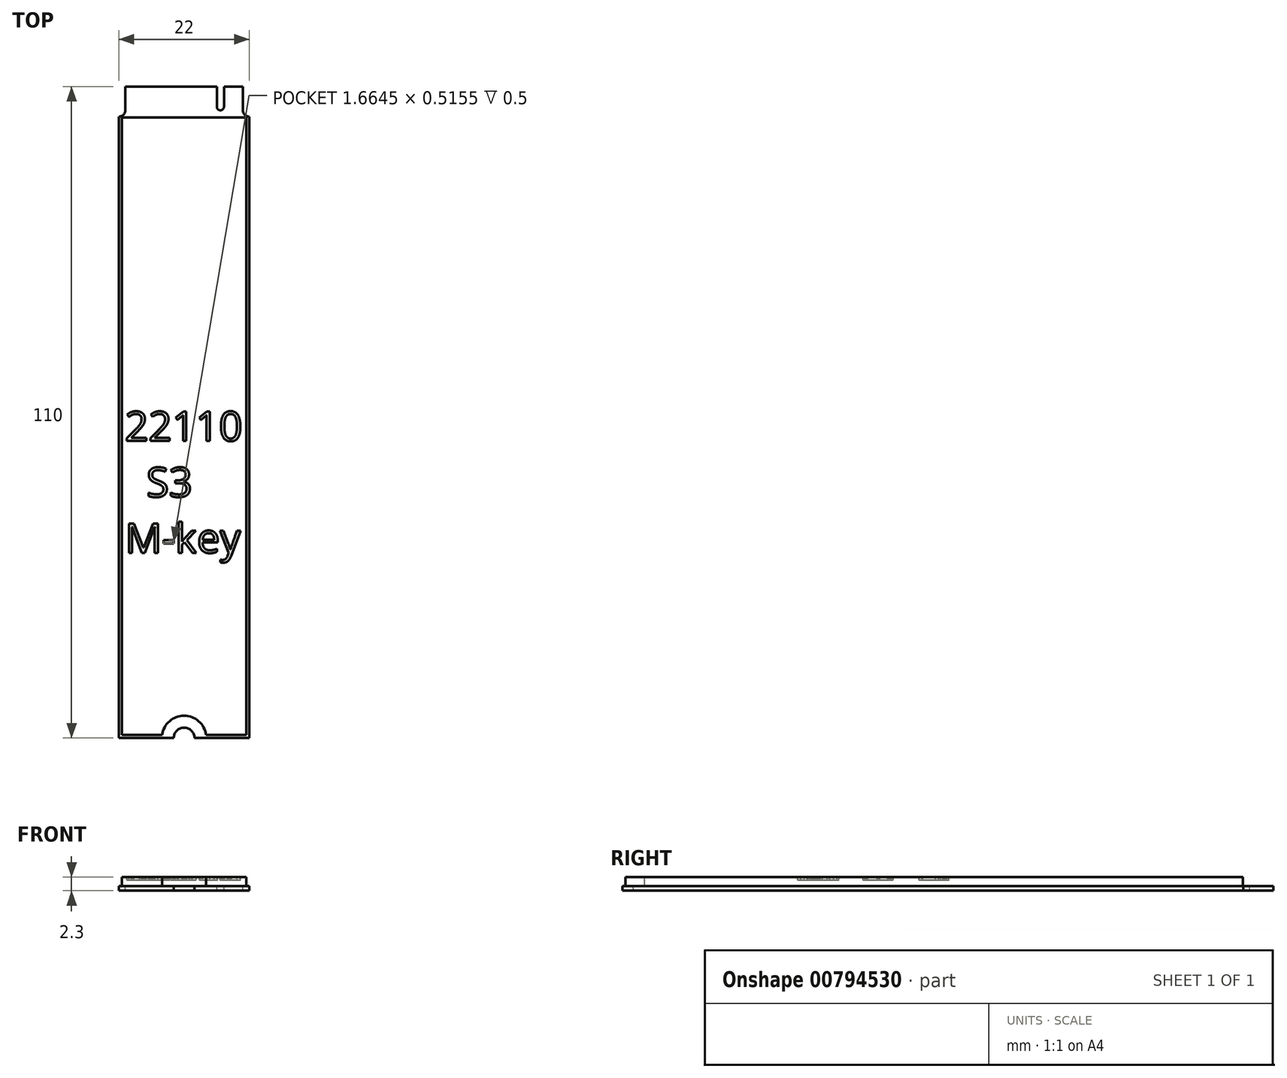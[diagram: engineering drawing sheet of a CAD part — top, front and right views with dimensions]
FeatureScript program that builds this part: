
annotation { "Feature Type Name" : "Feature", "Feature Type Description" : "" }
export const myFeature = defineFeature(function(context is Context, id is Id, definition is map)
    precondition{}
    {
        {
            assignVariable(context, id + "F0", {"name" : "thick", "anyValue" : .8});
        }
        {
            assignVariable(context, id + "F1", {"name" : "compheight", "anyValue" : 1.5});
        }
        {
            var Q0;
            Q0=qCreatedBy(makeId("Top.planeOp"),FACE);
            var sketch = newSketch(context, id + "F2", { "sketchPlane" : qUnion([Q0])});
            skLineSegment(sketch, "E0.bottom", {"start": v(-11, 55) * mm, "end": v(11, 55) * mm});
            skLineSegment(sketch, "E0.top", {"start": v(-11, -55) * mm, "end": v(11, -55) * mm});
            skLineSegment(sketch, "E0.left", {"start": v(-11, 55) * mm, "end": v(-11, -55) * mm});
            skLineSegment(sketch, "E0.right", {"start": v(11, 55) * mm, "end": v(11, -55) * mm});
            skPoint(sketch, "E0.middle", {"position": v(0, 0) * mm});
            skSolve(sketch);
        }
        {
            var Q0;
            Q0=qSketchRegion(id+"F2",true);
            extrude(context, id + "F3", {"entities" : qUnion([Q0]), "depth" : (getVariable(context, 'thick')) * mm});
        }
        {
            var Q0;
            Q0=makeQuery(id+"F3.opExtrude","CAP_FACE",FACE,{"disambiguationData":[OSD([sQuery(id+"F2.wireOp",EDGE,"E0.bottom"),sQuery(id+"F2.wireOp",EDGE,"E0.top"),sQuery(id+"F2.wireOp",EDGE,"E0.left"),sQuery(id+"F2.wireOp",EDGE,"E0.right")])],"isStart":false});
            var sketch = newSketch(context, id + "F4", { "sketchPlane" : qUnion([Q0])});
            skLineSegment(sketch, "E1.bottom", {"start": v(-10.5, -54.5) * mm, "end": v(10.5, -54.5) * mm});
            skLineSegment(sketch, "E1.top", {"start": v(-10.5, 49.8) * mm, "end": v(10.5, 49.8) * mm});
            skLineSegment(sketch, "E1.left", {"start": v(-10.5, -54.5) * mm, "end": v(-10.5, 49.8) * mm});
            skLineSegment(sketch, "E1.right", {"start": v(10.5, -54.5) * mm, "end": v(10.5, 49.8) * mm});
            skLineSegment(sketch, "E2", {"start": v(0, -55) * mm, "end": v(0, -54.5) * mm, "construction": true});
            skLineSegment(sketch, "E3", {"start": v(10.5, -2.35) * mm, "end": v(11, -2.35) * mm, "construction": true});
            skLineSegment(sketch, "E4", {"start": v(0, 49.8) * mm, "end": v(0, 55) * mm, "construction": true});
            skSolve(sketch);
        }
        {
            var Q0;
            Q0=qSketchRegion(id+"F4",true);
            extrude(context, id + "F5", {"entities" : qUnion([Q0]), "operationType" : NewBodyOperationType.ADD, "depth" : (getVariable(context, 'compheight')) * mm});
        }
        {
            var Q0;
            Q0=makeQuery(id+"F3.opExtrude","CAP_FACE",FACE,{"disambiguationData":[OSD([sQuery(id+"F2.wireOp",EDGE,"E0.bottom"),sQuery(id+"F2.wireOp",EDGE,"E0.top"),sQuery(id+"F2.wireOp",EDGE,"E0.left"),sQuery(id+"F2.wireOp",EDGE,"E0.right")])],"isStart":false});
            var sketch = newSketch(context, id + "F6", { "sketchPlane" : qUnion([Q0])});
            skLineSegment(sketch, "E5", {"start": v(0, 55) * mm, "end": v(0, 49.8) * mm, "construction": true});
            skLineSegment(sketch, "E6", {"start": v(-9.92, 55) * mm, "end": v(-9.92, 51) * mm});
            skArc(sketch, "E7", {"start": v(-11, 49.92) * mm, "mid": v(-10.24, 50.24) * mm, "end": v(-9.92, 51) * mm});
            skLineSegment(sketch, "E8", {"start": v(-9.92, 55) * mm, "end": v(-11, 55) * mm});
            skLineSegment(sketch, "E9", {"start": v(-11, 55) * mm, "end": v(-11, 49.92) * mm});
            skLineSegment(sketch, "E10.MirrorCS", {"start": v(9.93, 55) * mm, "end": v(9.93, 51) * mm});
            skLineSegment(sketch, "E11.MirrorCS", {"start": v(9.92, 55) * mm, "end": v(11, 55) * mm});
            skLineSegment(sketch, "E12.MirrorCS", {"start": v(11, 55) * mm, "end": v(11, 49.92) * mm});
            skArc(sketch, "E13.MirrorCS", {"start": v(11, 49.92) * mm, "mid": v(10.24, 50.24) * mm, "end": v(9.92, 51) * mm});
            skLineSegment(sketch, "E14", {"start": v(-9.92, 55) * mm, "end": v(9.92, 55) * mm, "construction": true});
            skLineSegment(sketch, "E15", {"start": v(0, 55) * mm, "end": v(6.13, 55) * mm, "construction": true});
            skLineSegment(sketch, "E16", {"start": v(6.13, 55) * mm, "end": v(6.13, 51.6) * mm, "construction": true});
            skLineSegment(sketch, "E17", {"start": v(0, 55) * mm, "end": v(-5.63, 55) * mm, "construction": true});
            skLineSegment(sketch, "E18", {"start": v(-9.92, 51) * mm, "end": v(6.13, 51) * mm, "construction": true});
            skArc(sketch, "E19", {"start": v(5.53, 51.6) * mm, "mid": v(6.13, 51) * mm, "end": v(6.73, 51.6) * mm});
            skLineSegment(sketch, "E20", {"start": v(6.13, 51.6) * mm, "end": v(5.53, 51.6) * mm, "construction": true});
            skLineSegment(sketch, "E21", {"start": v(6.73, 51.6) * mm, "end": v(6.73, 55) * mm});
            skLineSegment(sketch, "E22", {"start": v(6.73, 55) * mm, "end": v(5.53, 55) * mm});
            skLineSegment(sketch, "E23", {"start": v(5.53, 55) * mm, "end": v(5.53, 51.6) * mm});
            skLineSegment(sketch, "E24", {"start": v(-6.23, 55) * mm, "end": v(-6.23, 26.62) * mm, "construction": true});
            skLineSegment(sketch, "E25", {"start": v(-5.03, 55) * mm, "end": v(-5.03, 26.62) * mm, "construction": true});
            skArc(sketch, "E26", {"start": v(-6.23, 26.62) * mm, "mid": v(-5.63, 26.02) * mm, "end": v(-5.03, 26.62) * mm, "construction": true});
            skLineSegment(sketch, "E27", {"start": v(-6.23, 26.62) * mm, "end": v(-5.03, 26.62) * mm, "construction": true});
            skLineSegment(sketch, "E28", {"start": v(-5.63, 55) * mm, "end": v(-5.63, 26.62) * mm, "construction": true});
            skLineSegment(sketch, "E29", {"start": v(-6.23, 55) * mm, "end": v(-5.03, 55) * mm});
            skSolve(sketch);
        }
        {
            var Q0;
            Q0=qSketchRegion(id+"F6",true);
            extrude(context, id + "F7", {"entities" : qUnion([Q0]), "operationType" : NewBodyOperationType.REMOVE, "endBound" : BoundingType.THROUGH_ALL, "oppositeDirection" : true, "depth" : 25 * mm});
        }
        {
            var Q0;
            Q0=makeQuery(id+"F3.opExtrude","CAP_FACE",FACE,{"disambiguationData":[OSD([sQuery(id+"F2.wireOp",EDGE,"E0.bottom"),sQuery(id+"F2.wireOp",EDGE,"E0.top"),sQuery(id+"F2.wireOp",EDGE,"E0.left"),sQuery(id+"F2.wireOp",EDGE,"E0.right")])],"isStart":true});
            var sketch = newSketch(context, id + "F8", { "sketchPlane" : qUnion([Q0])});
            skCircle(sketch, "E30", {"center": v(0, 55) * mm, "radius": 1.75 * mm});
            skSolve(sketch);
        }
        {
            var Q0;
            Q0=qSketchRegion(id+"F8",true);
            extrude(context, id + "F9", {"entities" : qUnion([Q0]), "operationType" : NewBodyOperationType.REMOVE, "endBound" : BoundingType.THROUGH_ALL, "oppositeDirection" : true, "depth" : 25 * mm});
        }
        {
            var Q0;
            Q0=makeQuery(id+"F5.opExtrude","CAP_FACE",FACE,{"disambiguationData":[OSD([sQuery(id+"F4.wireOp",EDGE,"E1.bottom"),sQuery(id+"F4.wireOp",EDGE,"E1.top"),sQuery(id+"F4.wireOp",EDGE,"E1.left"),sQuery(id+"F4.wireOp",EDGE,"E1.right")])],"isStart":false});
            var sketch = newSketch(context, id + "F10", { "sketchPlane" : qUnion([Q0])});
            skArc(sketch, "E31.0", {"start": v(1.68, -54.5) * mm, "mid": v(0, -53.25) * mm, "end": v(-1.68, -54.5) * mm});
            skArc(sketch, "E32.0", {"start": v(3.72, -54.5) * mm, "mid": v(0, -51.25) * mm, "end": v(-3.72, -54.5) * mm});
            skLineSegment(sketch, "E33", {"start": v(-1.68, -54.5) * mm, "end": v(-3.72, -54.5) * mm});
            skLineSegment(sketch, "E34", {"start": v(1.68, -54.5) * mm, "end": v(3.72, -54.5) * mm});
            skSolve(sketch);
        }
        {
            var Q0;
            Q0=qSketchRegion(id+"F10",true);
            var Q1;
            Q1=makeQuery(id+"F3.opExtrude","CAP_FACE",FACE,{"disambiguationData":[OSD([sQuery(id+"F2.wireOp",EDGE,"E0.bottom"),sQuery(id+"F2.wireOp",EDGE,"E0.top"),sQuery(id+"F2.wireOp",EDGE,"E0.left"),sQuery(id+"F2.wireOp",EDGE,"E0.right")])],"isStart":false});
            extrude(context, id + "F11", {"entities" : qUnion([Q0]), "operationType" : NewBodyOperationType.REMOVE, "endBound" : BoundingType.UP_TO_SURFACE, "oppositeDirection" : true, "endBoundEntityFace" : qUnion([Q1]), "depth" : 25 * mm});
        }
        {
            var Q0;
            Q0=makeQuery(id+"F5.opExtrude","CAP_FACE",FACE,{"disambiguationData":[OSD([sQuery(id+"F4.wireOp",EDGE,"E1.bottom"),sQuery(id+"F4.wireOp",EDGE,"E1.top"),sQuery(id+"F4.wireOp",EDGE,"E1.left"),sQuery(id+"F4.wireOp",EDGE,"E1.right")])],"isStart":false});
            var sketch = newSketch(context, id + "F12", { "sketchPlane" : qUnion([Q0])});
            skLineSegment(sketch, "E35", {"start": v(10.5, -54.5) * mm, "end": v(-10.5, 49.8) * mm, "construction": true});
            skText(sketch, "E36", { "text": "22110\n  S3\nM-key", "fontName": "OpenSans-Regular.ttf"});
            skPoint(sketch, "E37", {"position": v(0, -2.35) * mm});
            const initialGuessF12  = {"E36": [-0.01, -0.00485, 1, 0, 0.005]};
            skSetInitialGuess(sketch, initialGuessF12);
            skSolve(sketch);
        }
        {
            var Q0;
            Q0=qSketchRegion(id+"F12",true);
            extrude(context, id + "F13", {"entities" : qUnion([Q0]), "operationType" : NewBodyOperationType.REMOVE, "oppositeDirection" : true, "depth" : .5 * mm});
        }
    });
